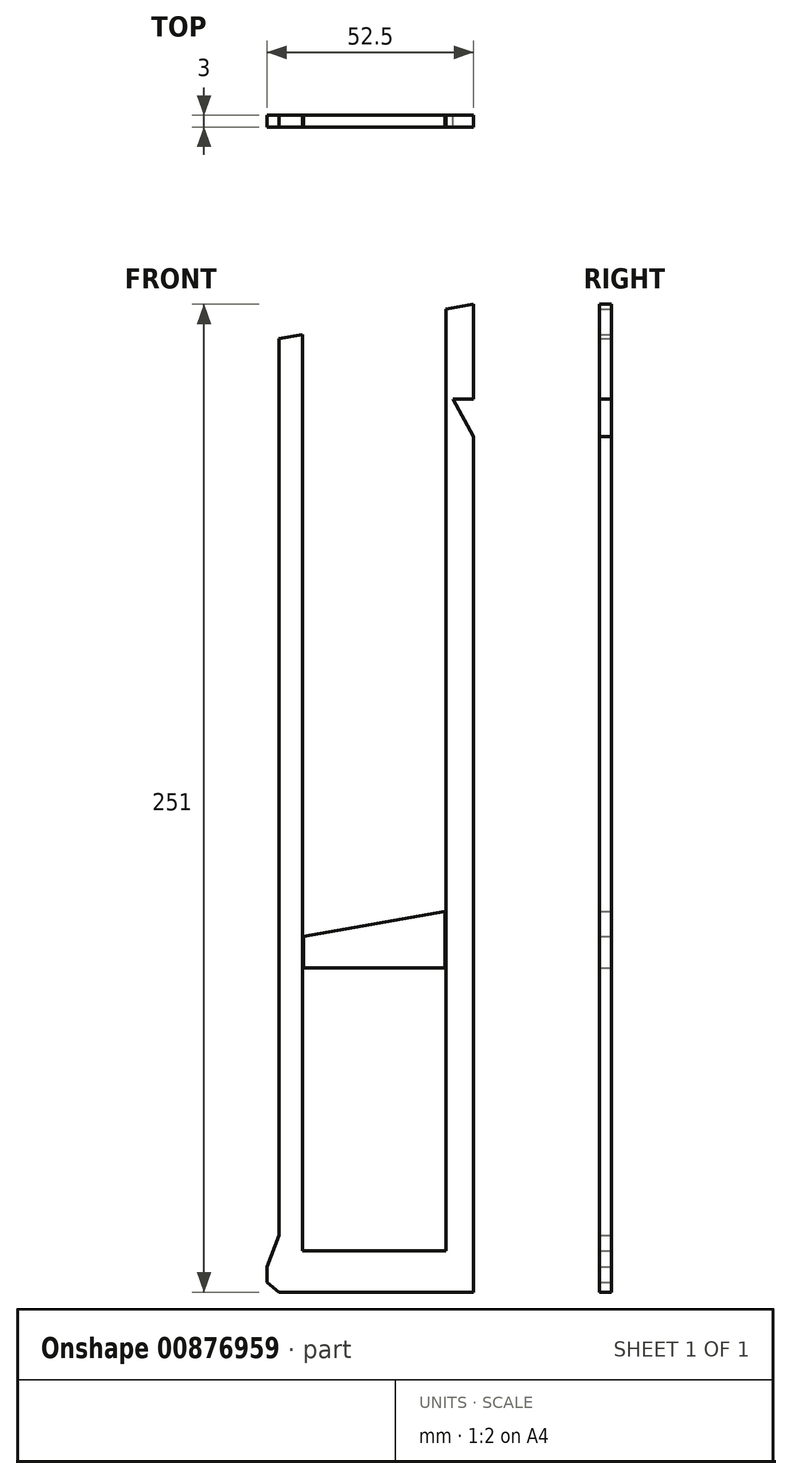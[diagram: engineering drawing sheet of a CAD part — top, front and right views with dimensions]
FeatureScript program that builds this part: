
annotation { "Feature Type Name" : "Feature", "Feature Type Description" : "" }
export const myFeature = defineFeature(function(context is Context, id is Id, definition is map)
    precondition{}
    {
        {
            var Q0;
            Q0=qCreatedBy(makeId("Front.planeOp"),FACE);
            var sketch = newSketch(context, id + "F0", { "sketchPlane" : qUnion([Q0])});
            skLineSegment(sketch, "E0", {"start": v(0, -251) * mm, "end": v(-49.5, -251) * mm});
            skPoint(sketch, "E1", {"position": v(-43.44, -7.66) * mm});
            skPoint(sketch, "E2", {"position": v(-7, -1.23) * mm});
            skLineSegment(sketch, "E3", {"start": v(-49.5, -8.73) * mm, "end": v(-43.44, -7.66) * mm});
            skLineSegment(sketch, "E4", {"start": v(0, 0) * mm, "end": v(-7, -1.23) * mm});
            skLineSegment(sketch, "E5", {"start": v(-43.44, -7.66) * mm, "end": v(-43.44, -240.5) * mm});
            skLineSegment(sketch, "E6", {"start": v(-7, -1.23) * mm, "end": v(-7, -240.5) * mm});
            skLineSegment(sketch, "E7", {"start": v(-7, -240.5) * mm, "end": v(-43.44, -240.5) * mm});
            skLineSegment(sketch, "E8", {"start": v(-43.19, -168.59) * mm, "end": v(-7.25, -168.59) * mm});
            skLineSegment(sketch, "E9", {"start": v(-43.19, -168.59) * mm, "end": v(-43.19, -160.59) * mm});
            skLineSegment(sketch, "E10", {"start": v(-43.19, -160.59) * mm, "end": v(-7.25, -154.25) * mm});
            skLineSegment(sketch, "E11", {"start": v(-7.25, -154.25) * mm, "end": v(-7.25, -168.59) * mm});
            skPoint(sketch, "E12", {"position": v(0, -24.07) * mm});
            skPoint(sketch, "E13", {"position": v(0, -33.57) * mm});
            skLineSegment(sketch, "E14", {"start": v(0, -24.07) * mm, "end": v(-5.25, -24.07) * mm});
            skLineSegment(sketch, "E15", {"start": v(-5.25, -24.07) * mm, "end": v(0, -33.57) * mm});
            skLineSegment(sketch, "E16", {"start": v(0, -24.07) * mm, "end": v(0, 0) * mm});
            skLineSegment(sketch, "E17", {"start": v(0, -33.57) * mm, "end": v(0, -251) * mm});
            skLineSegment(sketch, "E18", {"start": v(-49.5, -236.5) * mm, "end": v(-52.5, -244.5) * mm});
            skLineSegment(sketch, "E19", {"start": v(-52.5, -244.5) * mm, "end": v(-52.5, -248.5) * mm});
            skLineSegment(sketch, "E20", {"start": v(-52.5, -248.5) * mm, "end": v(-49.5, -251) * mm});
            skLineSegment(sketch, "E21", {"start": v(-49.5, -236.5) * mm, "end": v(-49.5, -8.73) * mm});
            skSolve(sketch);
        }
        {
            var Q0;
            Q0=makeQuery(id+"F0.imprint","IMPRINT",FACE,{"disambiguationData":[TD([[makeQuery(id+"F0.imprint","IMPRINT",EDGE,{"derivedFrom":sQuery(id+"F0.wireOp",EDGE,"ZOjMvmvA-9yqH-GHR5-0Tow-drmrUjQdXzBV")}),-1.0]])]});
            var Q1;
            Q1=makeQuery(id+"F0.imprint","IMPRINT",FACE,{"disambiguationData":[TD([[makeQuery(id+"F0.imprint","IMPRINT",EDGE,{"derivedFrom":sQuery(id+"F0.wireOp",EDGE,"E8")}),1.0]])]});
            extrude(context, id + "F1", {"entities" : qUnion([Q0, Q1]), "depth" : 3 * mm, "offsetDistance" : 25 * mm});
        }
        {
            var Q0;
            Q0=makeQuery(id+"F0.imprint","IMPRINT",FACE,{"disambiguationData":[TD([[makeQuery(id+"F0.imprint","IMPRINT",EDGE,{"derivedFrom":sQuery(id+"F0.wireOp",EDGE,"E0")}),-1.0]])]});
            extrude(context, id + "F2", {"entities" : qUnion([Q0]), "depth" : 3 * mm, "offsetDistance" : 25 * mm});
        }
    });
